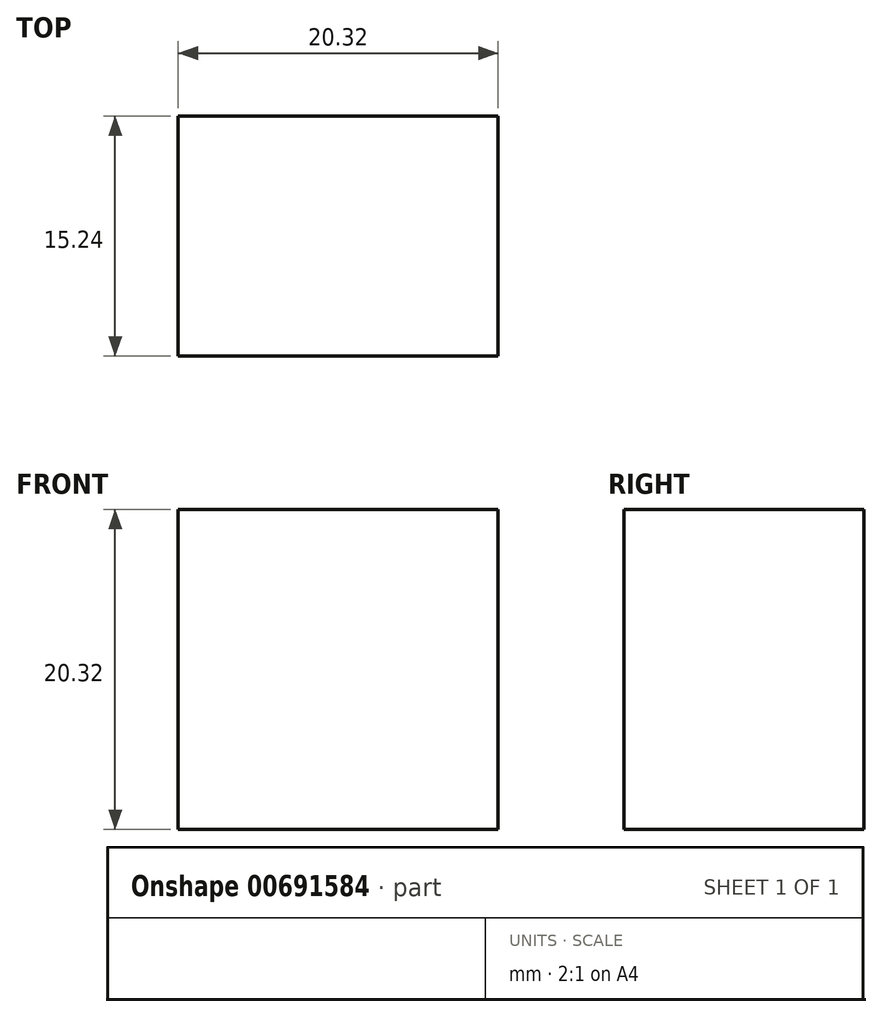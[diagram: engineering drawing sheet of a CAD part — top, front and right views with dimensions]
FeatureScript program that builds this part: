
annotation { "Feature Type Name" : "Feature", "Feature Type Description" : "" }
export const myFeature = defineFeature(function(context is Context, id is Id, definition is map)
    precondition{}
    {
        {
            var Q0;
            Q0=qCreatedBy(makeId("Front.planeOp"),FACE);
            var sketch = newSketch(context, id + "F0", { "sketchPlane" : qUnion([Q0])});
            skLineSegment(sketch, "E0.bottom", {"start": v(0, 20.32) * mm, "end": v(20.32, 20.32) * mm});
            skLineSegment(sketch, "E0.top", {"start": v(0, 0) * mm, "end": v(20.32, 0) * mm});
            skLineSegment(sketch, "E0.left", {"start": v(0, 20.32) * mm, "end": v(0, 0) * mm});
            skLineSegment(sketch, "E0.right", {"start": v(20.32, 20.32) * mm, "end": v(20.32, 0) * mm});
            skSolve(sketch);
        }
        {
            var Q0;
            Q0=makeQuery(id+"F0.imprint","IMPRINT",FACE,{"disambiguationData":[TD([[makeQuery(id+"F0.imprint","IMPRINT",EDGE,{"derivedFrom":sQuery(id+"F0.wireOp",EDGE,"E0.bottom")}),-1.0]])]});
            extrude(context, id + "F1", {"entities" : qUnion([Q0]), "depth" : 15.24 * mm, "offsetDistance" : 25.4 * mm});
        }
    });
